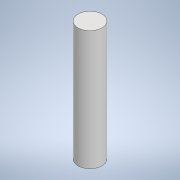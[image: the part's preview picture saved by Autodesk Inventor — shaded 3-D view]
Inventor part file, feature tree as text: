
AUTODESK INVENTOR PART (.ipt)
format: ipt  version: 2023 (Build 270158000, 158)  size: 91,136 bytes
history: native  units: mm
features: extrude x1, sketch x1
ambient origin geometry x8: Origin, YZ Plane, XZ Plane, XY Plane, X Axis, Y Axis, Z Axis, Center Point
bodies: Solid1 (feature_tree)
feature tree (2):
  extrude  "Extrusion1"  Depth=10.0mm TaperAngle=0.0deg
  sketch  "Sketch1"  dims[d0=3.0mm d1=10.0mm d2=0.0mm]
